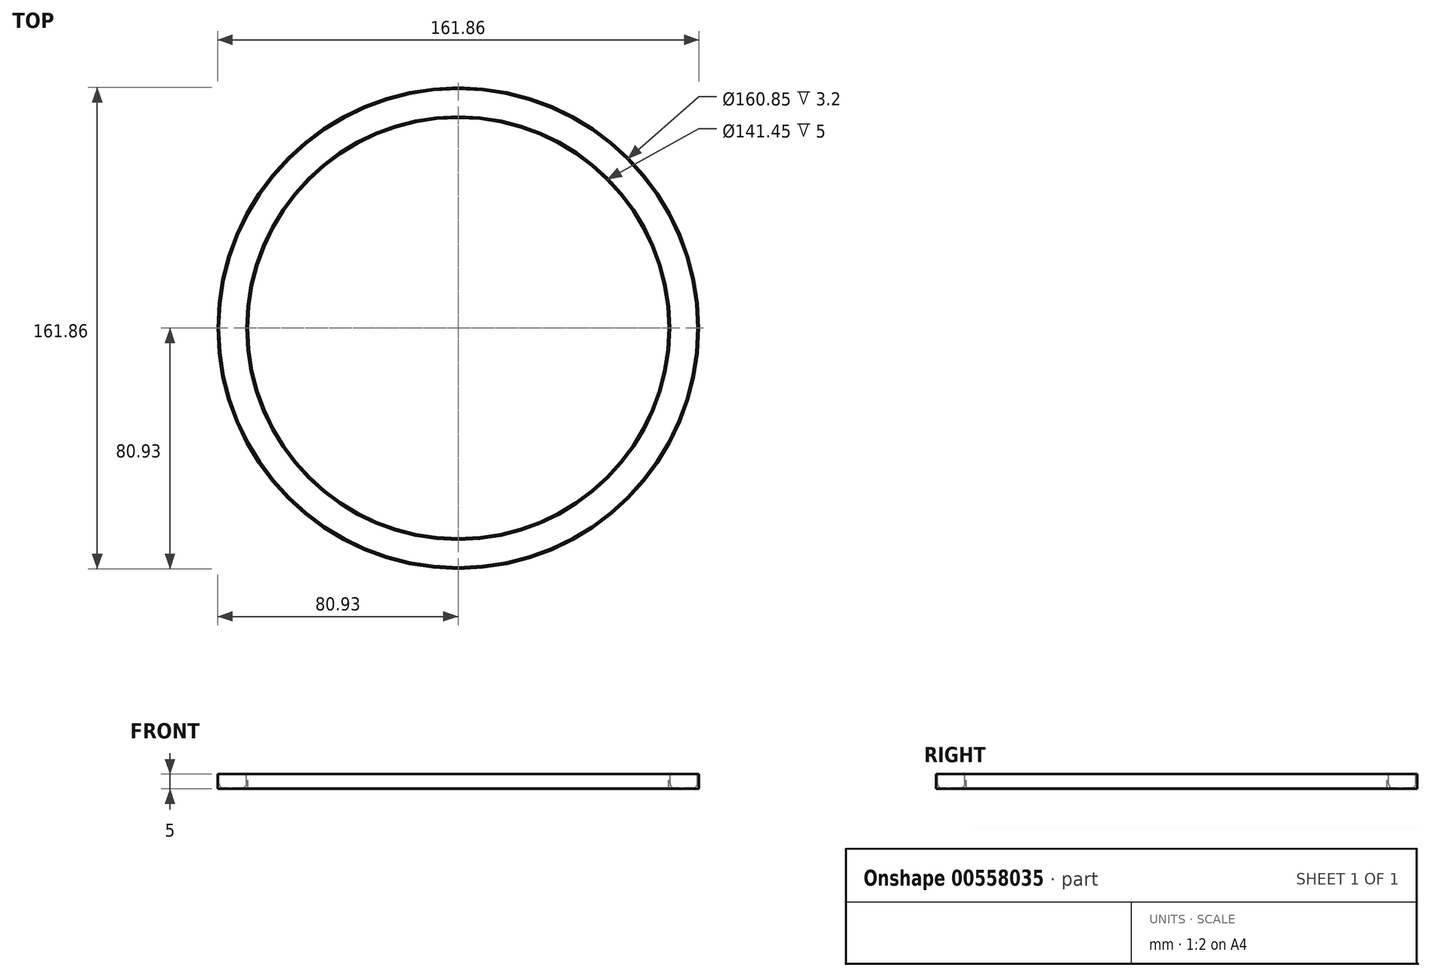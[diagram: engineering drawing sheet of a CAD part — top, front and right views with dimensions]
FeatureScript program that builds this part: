
annotation { "Feature Type Name" : "Feature", "Feature Type Description" : "" }
export const myFeature = defineFeature(function(context is Context, id is Id, definition is map)
    precondition{}
    {
        {
            var Q0;
            Q0=qCreatedBy(makeId("Front.planeOp"),FACE);
            var sketch = newSketch(context, id + "F0", { "sketchPlane" : qUnion([Q0])});
            skLineSegment(sketch, "E0", {"start": v(0, 0) * mm, "end": v(-115.72, 0) * mm, "construction": true});
            skPoint(sketch, "E1", {"position": v(-70.72, 0) * mm});
            skLineSegment(sketch, "E2", {"start": v(-70.72, 0) * mm, "end": v(-70.72, 5) * mm});
            skLineSegment(sketch, "E3", {"start": v(-70.72, 5) * mm, "end": v(-71.22, 5) * mm});
            skLineSegment(sketch, "E4", {"start": v(-71.22, 5) * mm, "end": v(-71.22, 0) * mm});
            skLineSegment(sketch, "E5", {"start": v(-71.22, 0) * mm, "end": v(-70.72, 0) * mm});
            skLineSegment(sketch, "E6", {"start": v(-71.22, 0.3) * mm, "end": v(-80.42, 0.3) * mm});
            skLineSegment(sketch, "E7", {"start": v(-80.42, 0.3) * mm, "end": v(-80.42, 0) * mm});
            skLineSegment(sketch, "E8", {"start": v(-80.42, 0) * mm, "end": v(-71.22, 0) * mm});
            skLineSegment(sketch, "E9", {"start": v(-80.42, 0.3) * mm, "end": v(-80.42, 5) * mm});
            skLineSegment(sketch, "E10", {"start": v(-80.42, 5) * mm, "end": v(-80.92, 5) * mm});
            skLineSegment(sketch, "E11", {"start": v(-80.92, 5) * mm, "end": v(-80.92, 0) * mm});
            skLineSegment(sketch, "E12", {"start": v(-80.92, 0) * mm, "end": v(-80.42, 0) * mm});
            skPoint(sketch, "E13", {"position": v(-75.83, 0.3) * mm});
            skLineSegment(sketch, "E14", {"start": v(-75.83, 8.08) * mm, "end": v(-75.83, -3.06) * mm, "construction": true});
            skLineSegment(sketch, "E15", {"start": v(-75.83, 3.3) * mm, "end": v(-75.83, 0.3) * mm});
            skSolve(sketch);
        }
        {
            var Q0;
            Q0=qCreatedBy(makeId("Front.planeOp"),FACE);
            var sketch = newSketch(context, id + "F1", { "sketchPlane" : qUnion([Q0])});
            skLineSegment(sketch, "E16", {"start": v(0, 53.88) * mm, "end": v(0, -46.31) * mm, "construction": true});
            skSolve(sketch);
        }
        {
            var Q0;
            Q0=makeQuery(id+"F0.imprint","IMPRINT",FACE,{"disambiguationData":[TD([[makeQuery(id+"F0.imprint","IMPRINT",EDGE,{"derivedFrom":sQuery(id+"F0.wireOp",EDGE,"E2")}),1.0]])]});
            var Q1;
            {var subQ2=sQuery(id+"F0.wireOp",EDGE,"E6");Q1=makeQuery(id+"F0.imprint","IMPRINT",FACE,{"disambiguationData":[TD([[makeQuery(id+"F0.imprint","IMPRINT",EDGE,{"derivedFrom":subQ2}),1.0]])]});}
            var Q2;
            Q2=makeQuery(id+"F0.imprint","IMPRINT",FACE,{"disambiguationData":[TD([[makeQuery(id+"F0.imprint","IMPRINT",EDGE,{"derivedFrom":sQuery(id+"F0.wireOp",EDGE,"E7")}),-1.0]])]});
            var Q3;
            Q3=sQuery(id+"F1.wireOp",EDGE,"E16");
            revolve(context, id + "F2", {"entities" : qUnion([Q0, Q1, Q2]), "axis" : qUnion([Q3]), "revolveType" : RevolveType.FULL});
        }
        {
            var Q0;
            Q0=makeQuery(id+"F2.opRevolve","SWEPT_EDGE",EDGE,{"disambiguationData":[OSD([sQuery(id+"F0.wireOp",EDGE,"E6"),sQuery(id+"F0.wireOp",EDGE,"E7"),sQuery(id+"F0.wireOp",EDGE,"E9")])]});
            var Q1;
            Q1=makeQuery(id+"F2.opRevolve","SWEPT_EDGE",EDGE,{"disambiguationData":[OSD([sQuery(id+"F0.wireOp",EDGE,"E4"),sQuery(id+"F0.wireOp",EDGE,"E6")])]});
            fillet(context, id + "F3", {"entities" : qUnion([Q0, Q1]), "radius" : 1.5 * mm, "tangentPropagation" : true, "allowEdgeOverflow" : false});
        }
    });
